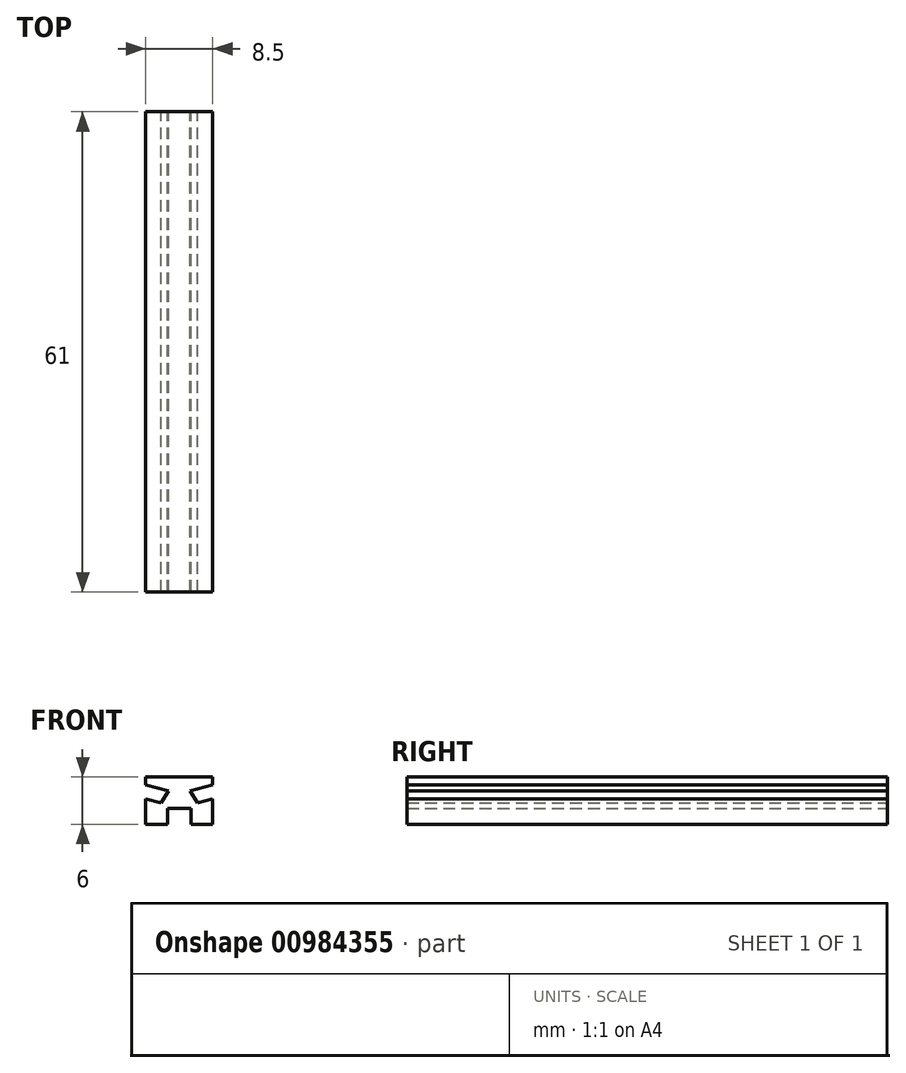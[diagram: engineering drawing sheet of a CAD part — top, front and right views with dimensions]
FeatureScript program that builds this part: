
annotation { "Feature Type Name" : "Feature", "Feature Type Description" : "" }
export const myFeature = defineFeature(function(context is Context, id is Id, definition is map)
    precondition{}
    {
        {
            var Q0;
            Q0=qCreatedBy(makeId("Front.planeOp"),FACE);
            var sketch = newSketch(context, id + "F0", { "sketchPlane" : qUnion([Q0])});
            skLineSegment(sketch, "E0.bottom", {"start": v(4.25, 3) * mm, "end": v(-4.25, 3) * mm});
            skLineSegment(sketch, "E0.top", {"start": v(4.25, -3) * mm, "end": v(-4.25, -3) * mm});
            skLineSegment(sketch, "E0.left", {"start": v(4.25, 3) * mm, "end": v(4.25, -3) * mm});
            skLineSegment(sketch, "E0.right", {"start": v(-4.25, 3) * mm, "end": v(-4.25, -3) * mm});
            skPoint(sketch, "E0.middle", {"position": v(0, 0) * mm});
            skLineSegment(sketch, "E1.bottom", {"start": v(-1.5, -3) * mm, "end": v(1.5, -3) * mm});
            skLineSegment(sketch, "E1.top", {"start": v(-1.5, -1) * mm, "end": v(1.5, -1) * mm});
            skLineSegment(sketch, "E1.left", {"start": v(-1.5, -3) * mm, "end": v(-1.5, -1) * mm});
            skLineSegment(sketch, "E1.right", {"start": v(1.5, -3) * mm, "end": v(1.5, -1) * mm});
            skPoint(sketch, "E1.middle", {"position": v(0, -2) * mm});
            skPoint(sketch, "E1.middle.positionSnap0", {"position": v(0, -3) * mm});
            skPoint(sketch, "E1.centerSnap0", {"position": v(0, -3) * mm});
            skLineSegment(sketch, "E2", {"start": v(4.25, 0.24) * mm, "end": v(2.32, -0.28) * mm});
            skLineSegment(sketch, "E3", {"start": v(1.35, 1.22) * mm, "end": v(4.25, 2) * mm});
            skLineSegment(sketch, "E4", {"start": v(1.35, 1.22) * mm, "end": v(2.32, -0.28) * mm});
            skLineSegment(sketch, "E5", {"start": v(-4.25, 0.24) * mm, "end": v(-2.32, -0.28) * mm});
            skLineSegment(sketch, "E6", {"start": v(-4.25, 2) * mm, "end": v(-1.35, 1.22) * mm});
            skLineSegment(sketch, "E7", {"start": v(-2.32, -0.28) * mm, "end": v(-1.35, 1.22) * mm});
            skSolve(sketch);
        }
        {
            var Q0;
            {var subQ4=sQuery(id+"F0.wireOp",EDGE,"E0.bottom");Q0=makeQuery(id+"F0.imprint","IMPRINT",FACE,{"disambiguationData":[TD([[makeQuery(id+"F0.imprint","IMPRINT",EDGE,{"derivedFrom":subQ4}),1.0]])]});}
            extrude(context, id + "F1", {"entities" : qUnion([Q0]), "depth" : 61 * mm, "offsetDistance" : 25 * mm});
        }
    });
